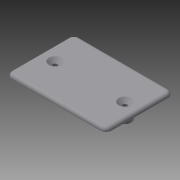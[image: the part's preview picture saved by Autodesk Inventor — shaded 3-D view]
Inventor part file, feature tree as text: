
AUTODESK INVENTOR PART (.ipt)
format: ipt  version: 2014 (Build 180170000, 170)  size: 118,272 bytes
history: native  units: mm
features: extrude x3, sketch x3, reference x3, fillet x1, chamfer x1
ambient origin geometry x8: Origin, YZ Plane, XZ Plane, XY Plane, X Axis, Y Axis, Z Axis, Center Point
bodies: Solid1 (feature_tree)
feature tree (11):
  extrude  "Extrusion1"  Depth=1.8mm TaperAngle=0.0deg
  extrude  "Extrusion2"  Depth=7.0mm
  extrude  "Extrusion3"  Depth=1.8mm
  fillet  "Fillet1"  Radius=2.0mm
  chamfer  "Chamfer1"  [1 undecoded]
  sketch  "Sketch1"  dims[d0=1.8mm d1=0.0mm d2=1.8mm d3=0.0mm]
  reference  "Reference1"
  sketch  "Sketch2"  dims[d4=7.0mm d5=7.0mm]
  reference  "Reference2"
  reference  "Reference3"
  sketch  "Sketch3"  dims[d6=6.05mm d7=0.0mm d8=1.8mm d9=2.0mm d10=2.0mm d11=45.0deg]
note: 1 required parameter value undecoded (feature->parameter linkage not recoverable at this tier; creation-order binding heuristic only, values carry confidence <= 0.55)
